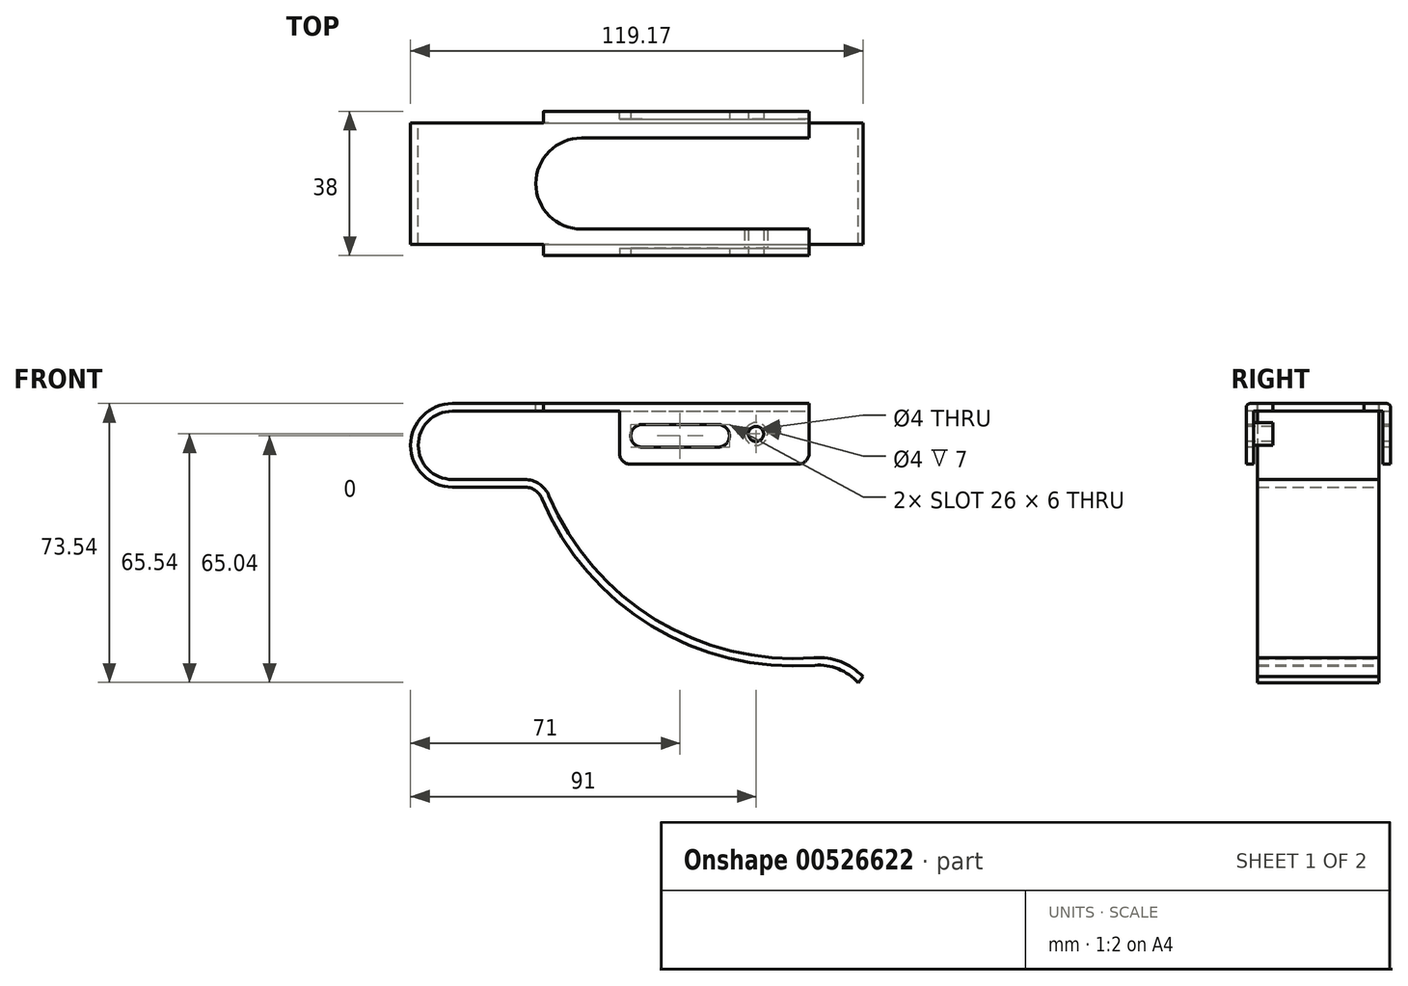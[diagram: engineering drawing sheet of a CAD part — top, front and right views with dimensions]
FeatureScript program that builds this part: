
annotation { "Feature Type Name" : "Feature", "Feature Type Description" : "" }
export const myFeature = defineFeature(function(context is Context, id is Id, definition is map)
    precondition{}
    {
        {
            var Q0;
            Q0=qCreatedBy(makeId("Front.planeOp"),FACE);
            var sketch = newSketch(context, id + "F0", { "sketchPlane" : qUnion([Q0])});
            skArc(sketch, "E0", {"start": v(0, 11) * mm, "mid": v(-11, 0) * mm, "end": v(0, -11) * mm});
            skLineSegment(sketch, "E1", {"start": v(0, -11) * mm, "end": v(19, -11) * mm});
            skArc(sketch, "E2", {"start": v(23.61, -14.06) * mm, "mid": v(52.44, -47.63) * mm, "end": v(95.45, -58) * mm});
            skLineSegment(sketch, "E3", {"start": v(0, 11) * mm, "end": v(94, 11) * mm});
            skArc(sketch, "E4", {"start": v(106.87, -62.54) * mm, "mid": v(101.69, -58.95) * mm, "end": v(95.45, -58) * mm});
            skPoint(sketch, "E5.visualSharp", {"position": v(22.4, -11) * mm});
            skArc(sketch, "E5.filletArc", {"start": v(23.61, -14.06) * mm, "mid": v(21.77, -11.84) * mm, "end": v(19, -11) * mm});
            skArc(sketch, "E6.0", {"start": v(108.17, -61) * mm, "mid": v(102.3, -57.04) * mm, "end": v(95.3, -56) * mm});
            skArc(sketch, "E6.1", {"start": v(25.45, -13.3) * mm, "mid": v(53.48, -45.92) * mm, "end": v(95.3, -56) * mm});
            skLineSegment(sketch, "E6.2", {"start": v(0, 9) * mm, "end": v(94, 9) * mm});
            skArc(sketch, "E6.3", {"start": v(0, 9) * mm, "mid": v(-9, 0) * mm, "end": v(0, -9) * mm});
            skLineSegment(sketch, "E6.4", {"start": v(0, -9) * mm, "end": v(19, -9) * mm});
            skArc(sketch, "E6.5", {"start": v(25.45, -13.3) * mm, "mid": v(22.88, -10.17) * mm, "end": v(19, -9) * mm});
            skLineSegment(sketch, "E7", {"start": v(94, 11) * mm, "end": v(94, 9) * mm});
            skLineSegment(sketch, "E8", {"start": v(108.17, -61) * mm, "end": v(106.87, -62.54) * mm});
            skLineSegment(sketch, "E9", {"start": v(112.4, -61) * mm, "end": v(117.08, -61) * mm});
            skSolve(sketch);
        }
        {
            var Q0;
            Q0=qSketchRegion(id+"F0",true);
            extrude(context, id + "F1", {"entities" : qUnion([Q0]), "depth" : 16 * mm});
        }
        {
            var Q0;
            Q0=makeQuery(id+"F1.opExtrude","SWEPT_FACE",FACE,{"disambiguationData":[OSD([sQuery(id+"F0.wireOp",EDGE,"E3")])]});
            var sketch = newSketch(context, id + "F2", { "sketchPlane" : qUnion([Q0])});
            skLineSegment(sketch, "E10.bottom", {"start": v(24, -16) * mm, "end": v(94, -16) * mm});
            skLineSegment(sketch, "E10.top", {"start": v(24, -19) * mm, "end": v(94, -19) * mm});
            skLineSegment(sketch, "E10.left", {"start": v(24, -16) * mm, "end": v(24, -19) * mm});
            skLineSegment(sketch, "E10.right", {"start": v(94, -16) * mm, "end": v(94, -19) * mm});
            skSolve(sketch);
        }
        {
            var Q0;
            Q0=qSketchRegion(id+"F2",true);
            extrude(context, id + "F3", {"entities" : qUnion([Q0]), "operationType" : NewBodyOperationType.ADD, "oppositeDirection" : true, "depth" : 2 * mm});
        }
        {
            var Q0;
            Q0=makeQuery(id+"F3.opExtrude","SWEPT_FACE",FACE,{"disambiguationData":[OSD([sQuery(id+"F2.wireOp",EDGE,"E10.top")])]});
            var sketch = newSketch(context, id + "F4", { "sketchPlane" : qUnion([Q0])});
            skLineSegment(sketch, "E11.bottom", {"start": v(24, 9) * mm, "end": v(94, 9) * mm});
            skLineSegment(sketch, "E11.top", {"start": v(44, -5) * mm, "end": v(94, -5) * mm});
            skLineSegment(sketch, "E11.left", {"start": v(44, 9) * mm, "end": v(44, -5) * mm});
            skLineSegment(sketch, "E11.right", {"start": v(94, 9) * mm, "end": v(94, -5) * mm});
            skSolve(sketch);
        }
        {
            var Q0;
            Q0=qSketchRegion(id+"F4",true);
            extrude(context, id + "F5", {"entities" : qUnion([Q0]), "operationType" : NewBodyOperationType.ADD, "oppositeDirection" : true, "depth" : 2 * mm});
        }
        {
            var Q0;
            Q0=makeQuery(id+"F3.opExtrude","CAP_EDGE",EDGE,{"disambiguationData":[OSD([sQuery(id+"F2.wireOp",EDGE,"E10.top")])],"isStart":true});
            var Q1;
            Q1=makeQuery(id+"F5.opExtrude","CAP_EDGE",EDGE,{"disambiguationData":[OSD([sQuery(id+"F4.wireOp",EDGE,"E11.bottom")])],"isStart":false});
            fillet(context, id + "F6", {"entities" : qUnion([Q0, Q1]), "radius" : 1 * mm, "tangentPropagation" : true, "allowEdgeOverflow" : false});
        }
        {
            var Q0;
            Q0=makeQuery(id+"F1.opExtrude","SWEPT_BODY",BODY,{"disambiguationData":[OSD([sQuery(id+"F0.wireOp",EDGE,"E0"),sQuery(id+"F0.wireOp",EDGE,"E1"),sQuery(id+"F0.wireOp",EDGE,"E2"),sQuery(id+"F0.wireOp",EDGE,"E3"),sQuery(id+"F0.wireOp",EDGE,"E4"),sQuery(id+"F0.wireOp",EDGE,"E5.filletArc"),sQuery(id+"F0.wireOp",EDGE,"E6.0"),sQuery(id+"F0.wireOp",EDGE,"E6.1"),sQuery(id+"F0.wireOp",EDGE,"E6.2"),sQuery(id+"F0.wireOp",EDGE,"E6.3"),sQuery(id+"F0.wireOp",EDGE,"E6.4"),sQuery(id+"F0.wireOp",EDGE,"E6.5"),sQuery(id+"F0.wireOp",EDGE,"E7"),sQuery(id+"F0.wireOp",EDGE,"E8")])]});
            var Q1;
            Q1=qCreatedBy(makeId("Front.planeOp"),FACE);
            mirror(context, id + "F7", {"operationType" : NewBodyOperationType.ADD, "entities" : qUnion([Q0]), "mirrorPlane" : qUnion([Q1])});
        }
        {
            var Q0;
            {var subQ0=makeQuery(id+"F3.boolean.opBoolean","MERGE",FACE,{"derivedFrom":[makeQuery(id+"F1.opExtrude","SWEPT_FACE",FACE,{"disambiguationData":[OSD([sQuery(id+"F0.wireOp",EDGE,"E3")])]}),makeQuery(id+"F3.opExtrude","CAP_FACE",FACE,{"disambiguationData":[OSD([sQuery(id+"F2.wireOp",EDGE,"E10.bottom"),sQuery(id+"F2.wireOp",EDGE,"E10.top"),sQuery(id+"F2.wireOp",EDGE,"E10.left"),sQuery(id+"F2.wireOp",EDGE,"E10.right")])],"isStart":true})]});Q0=makeQuery(id+"F7.boolean.opBoolean","MERGE",FACE,{"derivedFrom":[subQ0,makeQuery(id+"F7.opPattern","COPY",FACE,{"derivedFrom":subQ0,"instanceName":"1"})]});}
            var sketch = newSketch(context, id + "F8", { "sketchPlane" : qUnion([Q0])});
            skArc(sketch, "E12", {"start": v(34, 12) * mm, "mid": v(22, 0) * mm, "end": v(34, -12) * mm});
            skLineSegment(sketch, "E13", {"start": v(94, 16) * mm, "end": v(94, -16) * mm});
            skLineSegment(sketch, "E14", {"start": v(34, -12) * mm, "end": v(94, -12) * mm});
            skLineSegment(sketch, "E15", {"start": v(34, 12) * mm, "end": v(94, 12) * mm});
            skLineSegment(sketch, "E16", {"start": v(94, 12) * mm, "end": v(94, -12) * mm});
            skSolve(sketch);
        }
        {
            var Q0;
            Q0=qSketchRegion(id+"F8",true);
            extrude(context, id + "F9", {"entities" : qUnion([Q0]), "operationType" : NewBodyOperationType.REMOVE, "oppositeDirection" : true, "depth" : 4 * mm});
        }
        {
            var Q0;
            Q0=makeQuery(id+"F5.boolean.opBoolean","MERGE",FACE,{"derivedFrom":[makeQuery(id+"F3.opExtrude","SWEPT_FACE",FACE,{"disambiguationData":[OSD([sQuery(id+"F2.wireOp",EDGE,"E10.top")])]}),makeQuery(id+"F5.opExtrude","CAP_FACE",FACE,{"disambiguationData":[OSD([sQuery(id+"F4.wireOp",EDGE,"E11.bottom"),sQuery(id+"F4.wireOp",EDGE,"E11.top"),sQuery(id+"F4.wireOp",EDGE,"E11.left"),sQuery(id+"F4.wireOp",EDGE,"E11.right")])],"isStart":true})]});
            var sketch = newSketch(context, id + "F10", { "sketchPlane" : qUnion([Q0])});
            skLineSegment(sketch, "E17", {"start": v(70, 2.5) * mm, "end": v(50, 2.5) * mm});
            skPoint(sketch, "E17.startSnap0", {"position": v(94, 2.5) * mm});
            skArc(sketch, "E18.0.startCap", {"start": v(70, 5.5) * mm, "mid": v(73, 2.5) * mm, "end": v(70, -0.5) * mm});
            skArc(sketch, "E18.0.endCap", {"start": v(50, -0.5) * mm, "mid": v(47, 2.5) * mm, "end": v(50, 5.5) * mm});
            skLineSegment(sketch, "E18.0.left", {"start": v(70, -0.5) * mm, "end": v(50, -0.5) * mm});
            skLineSegment(sketch, "E18.0.right", {"start": v(70, 5.5) * mm, "end": v(50, 5.5) * mm});
            skSolve(sketch);
        }
        {
            var Q0;
            Q0=qSketchRegion(id+"F10",true);
            extrude(context, id + "F11", {"entities" : qUnion([Q0]), "operationType" : NewBodyOperationType.REMOVE, "endBound" : BoundingType.THROUGH_ALL, "oppositeDirection" : true, "depth" : 25 * mm});
        }
        {
            var Q0;
            Q0=makeQuery(id+"F5.boolean.opBoolean","MERGE",FACE,{"derivedFrom":[makeQuery(id+"F3.opExtrude","SWEPT_FACE",FACE,{"disambiguationData":[OSD([sQuery(id+"F2.wireOp",EDGE,"E10.top")])]}),makeQuery(id+"F5.opExtrude","CAP_FACE",FACE,{"disambiguationData":[OSD([sQuery(id+"F4.wireOp",EDGE,"E11.bottom"),sQuery(id+"F4.wireOp",EDGE,"E11.top"),sQuery(id+"F4.wireOp",EDGE,"E11.left"),sQuery(id+"F4.wireOp",EDGE,"E11.right")])],"isStart":true})]});
            var sketch = newSketch(context, id + "F12", { "sketchPlane" : qUnion([Q0])});
            skPoint(sketch, "E19", {"position": v(80, 3) * mm});
            skSolve(sketch);
        }
        {
            var Q0;
            Q0=sQuery(id+"F12.wireOp",VERTEX,"E19");
            var Q1;
            Q1=makeQuery(id+"F1.opExtrude","SWEPT_BODY",BODY,{"disambiguationData":[OSD([sQuery(id+"F0.wireOp",EDGE,"E0"),sQuery(id+"F0.wireOp",EDGE,"E1"),sQuery(id+"F0.wireOp",EDGE,"E2"),sQuery(id+"F0.wireOp",EDGE,"E3"),sQuery(id+"F0.wireOp",EDGE,"E4"),sQuery(id+"F0.wireOp",EDGE,"E5.filletArc"),sQuery(id+"F0.wireOp",EDGE,"E6.0"),sQuery(id+"F0.wireOp",EDGE,"E6.1"),sQuery(id+"F0.wireOp",EDGE,"E6.2"),sQuery(id+"F0.wireOp",EDGE,"E6.3"),sQuery(id+"F0.wireOp",EDGE,"E6.4"),sQuery(id+"F0.wireOp",EDGE,"E6.5"),sQuery(id+"F0.wireOp",EDGE,"E7"),sQuery(id+"F0.wireOp",EDGE,"E8")])]});
            hole(context, id + "F13", {"style" : HoleStyle.SIMPLE, "endStyle" : HoleEndStyle.THROUGH, "holeDiameter" : 4 * mm, "isTappedThrough" : true, "tappedDepth" : 12 * mm, "tapClearance" : 3, "locations" : qUnion([Q0]), "scope" : qUnion([Q1])});
        }
        {
            var Q0;
            Q0=makeQuery(id+"F5.opExtrude","CAP_FACE",FACE,{"disambiguationData":[OSD([sQuery(id+"F4.wireOp",EDGE,"E11.bottom"),sQuery(id+"F4.wireOp",EDGE,"E11.top"),sQuery(id+"F4.wireOp",EDGE,"E11.left"),sQuery(id+"F4.wireOp",EDGE,"E11.right")])],"isStart":false});
            var sketch = newSketch(context, id + "F14", { "sketchPlane" : qUnion([Q0])});
            skCircle(sketch, "E20.0", {"center": v(-80, 3) * mm, "radius": 2 * mm});
            skCircle(sketch, "E21.0", {"center": v(-80, 3) * mm, "radius": 3 * mm});
            skSolve(sketch);
        }
        {
            var Q0;
            Q0=qSketchRegion(id+"F14",true);
            extrude(context, id + "F15", {"entities" : qUnion([Q0]), "operationType" : NewBodyOperationType.ADD, "depth" : 5 * mm});
        }
        {
            var Q0;
            Q0=makeQuery(id+"F7.opPattern","COPY",EDGE,{"derivedFrom":makeQuery(id+"F5.opExtrude","SWEPT_EDGE",EDGE,{"disambiguationData":[OSD([sQuery(id+"F4.wireOp",EDGE,"E11.top"),sQuery(id+"F4.wireOp",EDGE,"E11.right")])]}),"instanceName":"1"});
            var Q1;
            Q1=makeQuery(id+"F7.opPattern","COPY",EDGE,{"derivedFrom":makeQuery(id+"F5.opExtrude","SWEPT_EDGE",EDGE,{"disambiguationData":[OSD([sQuery(id+"F4.wireOp",EDGE,"E11.top"),sQuery(id+"F4.wireOp",EDGE,"E11.left")])]}),"instanceName":"1"});
            var Q2;
            Q2=makeQuery(id+"F5.opExtrude","SWEPT_EDGE",EDGE,{"disambiguationData":[OSD([sQuery(id+"F4.wireOp",EDGE,"E11.top"),sQuery(id+"F4.wireOp",EDGE,"E11.right")])]});
            var Q3;
            Q3=makeQuery(id+"F5.opExtrude","SWEPT_EDGE",EDGE,{"disambiguationData":[OSD([sQuery(id+"F4.wireOp",EDGE,"E11.top"),sQuery(id+"F4.wireOp",EDGE,"E11.left")])]});
            fillet(context, id + "F16", {"entities" : qUnion([Q0, Q1, Q2, Q3]), "radius" : 3 * mm, "tangentPropagation" : true, "allowEdgeOverflow" : false});
        }
    });
